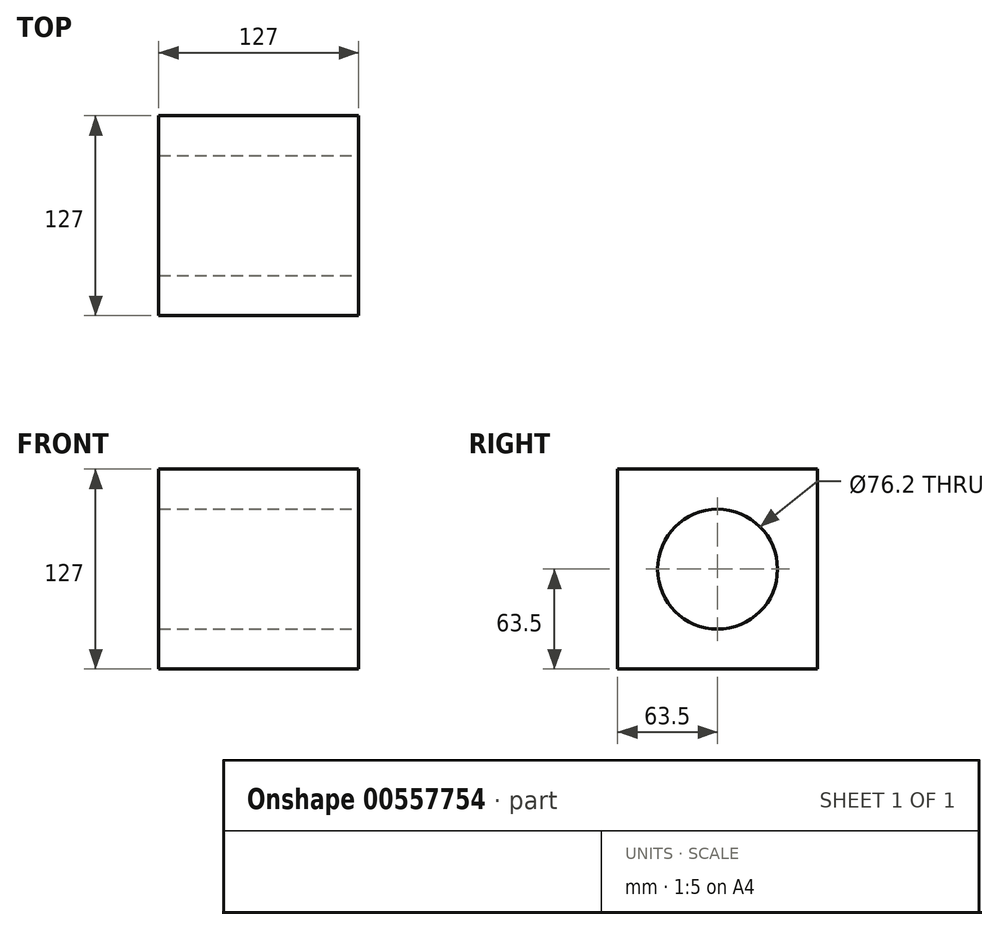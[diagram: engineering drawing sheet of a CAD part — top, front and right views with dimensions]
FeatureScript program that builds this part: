
annotation { "Feature Type Name" : "Feature", "Feature Type Description" : "" }
export const myFeature = defineFeature(function(context is Context, id is Id, definition is map)
    precondition{}
    {
        {
            var Q0;
            Q0=qCreatedBy(makeId("Front.planeOp"),FACE);
            var sketch = newSketch(context, id + "F0", { "sketchPlane" : qUnion([Q0])});
            skLineSegment(sketch, "E0", {"start": v(-43.04, 37.39) * mm, "end": v(83.96, 37.39) * mm});
            skLineSegment(sketch, "E1", {"start": v(83.96, 37.39) * mm, "end": v(83.96, -89.61) * mm});
            skLineSegment(sketch, "E2", {"start": v(83.96, -89.61) * mm, "end": v(-43.04, -89.61) * mm});
            skLineSegment(sketch, "E3", {"start": v(-43.04, -89.61) * mm, "end": v(-43.04, 37.39) * mm});
            skSolve(sketch);
        }
        {
            var Q0;
            Q0=makeQuery(id+"F0.imprint","IMPRINT",FACE,{"disambiguationData":[TD([[makeQuery(id+"F0.imprint","IMPRINT",EDGE,{"derivedFrom":sQuery(id+"F0.wireOp",EDGE,"E0")}),-1.0]])]});
            extrude(context, id + "F1", {"entities" : qUnion([Q0]), "oppositeDirection" : true, "depth" : 127 * mm, "offsetDistance" : 25.4 * mm});
        }
        {
            var Q0;
            Q0=makeQuery(id+"F1.opExtrude","SWEPT_FACE",FACE,{"disambiguationData":[OSD([sQuery(id+"F0.wireOp",EDGE,"E1")])]});
            var sketch = newSketch(context, id + "F2", { "sketchPlane" : qUnion([Q0])});
            skCircle(sketch, "E4", {"center": v(63.5, -26.11) * mm, "radius": 38.1 * mm});
            skPoint(sketch, "E4.centerSnap0", {"position": v(127, -26.11) * mm});
            skPoint(sketch, "E4.centerSnap1", {"position": v(63.5, 37.39) * mm});
            skSolve(sketch);
        }
        {
            var Q0;
            Q0=makeQuery(id+"F2.imprint","IMPRINT",FACE,{"disambiguationData":[TD([[makeQuery(id+"F2.imprint","IMPRINT",EDGE,{"derivedFrom":sQuery(id+"F2.wireOp",EDGE,"E4")}),1.0]])]});
            extrude(context, id + "F3", {"entities" : qUnion([Q0]), "operationType" : NewBodyOperationType.REMOVE, "endBound" : BoundingType.THROUGH_ALL, "oppositeDirection" : true, "depth" : 25.4 * mm, "offsetDistance" : 25.4 * mm});
        }
    });
